# Revit family: Vierteaguas H. C-1
name_source: partatom
category: Modelos genéricos
units: mm (PartAtom-declared; Revit-internal decimal feet)

## family parameters
Compartido = No
Corte con vacíos al cargar = No
Cota de conector redondo = Diámetro de uso
Puede alojar armadura = No
Punto de cálculo de habitación = No
Se basa en plano de trabajo = No
Siempre vertical = No
Tipo de pieza = Normal

## types (15) — shared parameters
Descripción = Pieza de hormigón polímero con anclaje de acero inoxidable.
Fabricante = ULMA Architectural Solutions
Material = Hormigón polímero STONEO. Color C-1
URL = https://www.ulmaarchitectural.com
zero-valued in all types: Elevación por defecto

## per-type parameters (varying)
| type | Ancho | Ancho doble | Ancho total | Modelo | Visible dos líneas | Visible una linea |
| H12 | 120 mm  [stored 0.393701 ft] | 30 mm  [stored 0.0984252 ft] | 145 mm  [stored 0.475722 ft] | Vierteaguas H12 | No | Sí |
| H14 | 140 mm  [stored 0.459318 ft] | 35 mm  [stored 0.114829 ft] | 165 mm | Vierteaguas H14 | No | Sí |
| H16 | 160 mm  [stored 0.524934 ft] | 40 mm  [stored 0.131234 ft] | 185 mm  [stored 0.606955 ft] | Vierteaguas H16 | No | Sí |
| H18 | 180 mm  [stored 0.590551 ft] | 45 mm  [stored 0.147638 ft] | 205 mm  [stored 0.672572 ft] | Vierteaguas H18 | No | Sí |
| H20 | 200 mm  [stored 0.656168 ft] | 50 mm  [stored 0.164042 ft] | 225 mm  [stored 0.738189 ft] | Vierteaguas H20 | No | Sí |
| H22 | 220 mm  [stored 0.721785 ft] | 55 mm  [stored 0.180446 ft] | 245 mm  [stored 0.803806 ft] | Vierteaguas H22 | No | Sí |
| H24 | 240 mm  [stored 0.787402 ft] | 60 mm  [stored 0.19685 ft] | 265 mm  [stored 0.869423 ft] | Vierteaguas H24 | No | Sí |
| H26 | 260 mm  [stored 0.853018 ft] | 65 mm  [stored 0.213255 ft] | 285 mm  [stored 0.935039 ft] | Vierteaguas H26 | No | Sí |
| H28 | 280 mm  [stored 0.918635 ft] | 70 mm  [stored 0.229659 ft] | 305 mm  [stored 1.00066 ft] | Vierteaguas H28 | No | Sí |
| H31 | 310 mm  [stored 1.01706 ft] | 78 mm | 335 mm  [stored 1.09908 ft] | Vierteaguas H31 | Sí | No |
| H34 | 340 mm  [stored 1.11549 ft] | 85 mm  [stored 0.278871 ft] | 365 mm  [stored 1.19751 ft] | Vierteaguas H34 | Sí | No |
| H37 | 370 mm  [stored 1.21391 ft] | 93 mm | 395 mm | Vierteaguas H37 | Sí | No |
| H39 | 390 mm  [stored 1.27953 ft] | 98 mm | 415 mm | Vierteaguas H39 | Sí | No |
| H43 | 430 mm | 108 mm | 455 mm | Vierteaguas H43 | Sí | No |
| H46 | 460 mm | 115 mm  [stored 0.377297 ft] | 485 mm | Vierteaguas H46 | Sí | No |

note: column(s) folded — value = type name in every type: Código de montaje

note: [stored X ft] marks values corroborated as IEEE doubles in the binary element streams (Revit-internal decimal feet)
